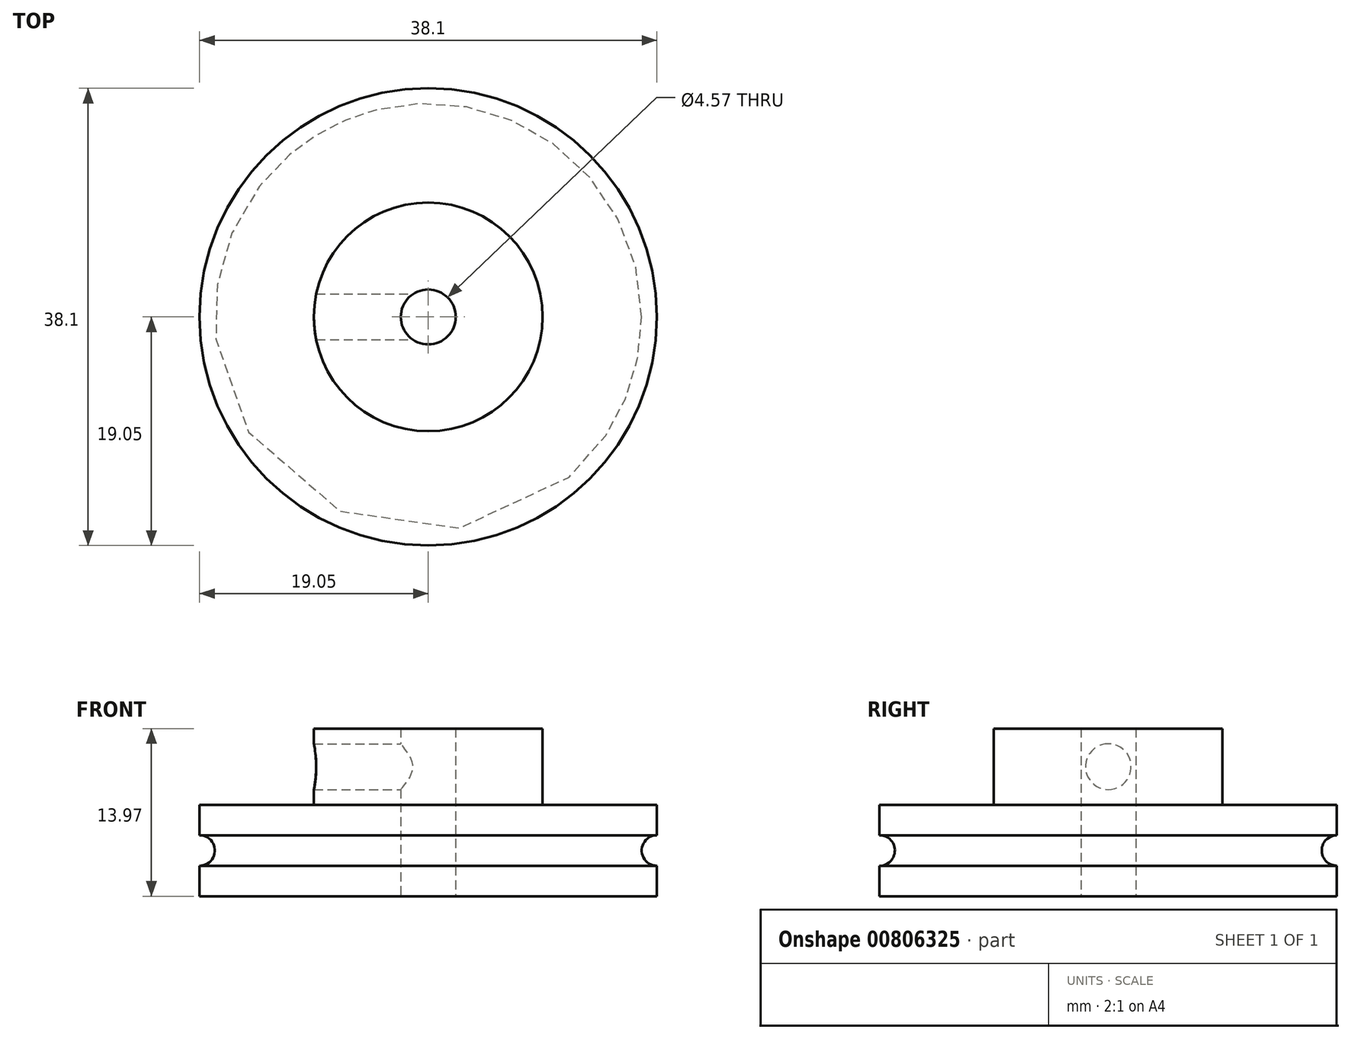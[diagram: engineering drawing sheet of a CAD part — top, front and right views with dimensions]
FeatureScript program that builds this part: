
annotation { "Feature Type Name" : "Feature", "Feature Type Description" : "" }
export const myFeature = defineFeature(function(context is Context, id is Id, definition is map)
    precondition{}
    {
        {
            var Q0;
            Q0=qCreatedBy(makeId("Top.planeOp"),FACE);
            var sketch = newSketch(context, id + "F0", { "sketchPlane" : qUnion([Q0])});
            skCircle(sketch, "E0", {"center": v(0, 0) * mm, "radius": 19.05 * mm});
            skSolve(sketch);
        }
        {
            var Q0;
            Q0=makeQuery(id+"F0.imprint","IMPRINT",FACE,{"disambiguationData":[TD([[makeQuery(id+"F0.imprint","IMPRINT",EDGE,{"derivedFrom":sQuery(id+"F0.wireOp",EDGE,"E0")}),1.0]])]});
            extrude(context, id + "F1", {"entities" : qUnion([Q0]), "depth" : 7.62 * mm, "offsetDistance" : 25.4 * mm});
        }
        {
            var Q0;
            Q0=makeQuery(id+"F1.opExtrude","CAP_FACE",FACE,{"disambiguationData":[OSD([sQuery(id+"F0.wireOp",EDGE,"E0")])],"isStart":false});
            var sketch = newSketch(context, id + "F2", { "sketchPlane" : qUnion([Q0])});
            skCircle(sketch, "E1", {"center": v(0, 0) * mm, "radius": 9.53 * mm});
            skSolve(sketch);
        }
        {
            var Q0;
            Q0=makeQuery(id+"F2.imprint","IMPRINT",FACE,{"disambiguationData":[TD([[makeQuery(id+"F2.imprint","IMPRINT",EDGE,{"derivedFrom":sQuery(id+"F2.wireOp",EDGE,"E1")}),1.0]])]});
            extrude(context, id + "F3", {"entities" : qUnion([Q0]), "operationType" : NewBodyOperationType.ADD, "depth" : 6.35 * mm, "offsetDistance" : 25.4 * mm});
        }
        {
            var Q0;
            Q0=qCreatedBy(makeId("Right.planeOp"),FACE);
            var sketch = newSketch(context, id + "F4", { "sketchPlane" : qUnion([Q0])});
            skCircle(sketch, "E2", {"center": v(0, 10.8) * mm, "radius": 1.9 * mm});
            skSolve(sketch);
        }
        {
            var Q0;
            Q0 = qSketchRegion(id + "F4", true);
            extrude(context, id + "F5", {"entities" : qUnion([Q0]), "operationType" : NewBodyOperationType.REMOVE, "oppositeDirection" : true, "depth" : 25.4 * mm, "offsetDistance" : 25.4 * mm});
        }
        {
            var Q0;
            Q0=makeQuery(id+"F1.opExtrude","CAP_FACE",FACE,{"disambiguationData":[OSD([sQuery(id+"F0.wireOp",EDGE,"E0")])],"isStart":true});
            var sketch = newSketch(context, id + "F6", { "sketchPlane" : qUnion([Q0])});
            skCircle(sketch, "E3", {"center": v(0, 0) * mm, "radius": 2.29 * mm});
            skSolve(sketch);
        }
        {
            var Q0;
            Q0=makeQuery(id+"F6.imprint","IMPRINT",FACE,{"disambiguationData":[TD([[makeQuery(id+"F6.imprint","IMPRINT",EDGE,{"derivedFrom":sQuery(id+"F6.wireOp",EDGE,"E3")}),1.0]])]});
            extrude(context, id + "F7", {"entities" : qUnion([Q0]), "operationType" : NewBodyOperationType.REMOVE, "oppositeDirection" : true, "depth" : 101.6 * mm, "offsetDistance" : 25.4 * mm});
        }
        {
            var Q0;
            Q0=qCreatedBy(makeId("Right.planeOp"),FACE);
            var sketch = newSketch(context, id + "F8", { "sketchPlane" : qUnion([Q0])});
            skCircle(sketch, "E4", {"center": v(-19.05, 3.81) * mm, "radius": 1.27 * mm});
            skSolve(sketch);
        }
        {
            var Q0;
            Q0=makeQuery(id+"F8.imprint","IMPRINT",FACE,{"disambiguationData":[TD([[makeQuery(id+"F8.imprint","IMPRINT",EDGE,{"derivedFrom":sQuery(id+"F8.wireOp",EDGE,"E4")}),1.0]])]});
            var Q1;
            Q1=makeQuery(id+"F3.opExtrude","CAP_EDGE",EDGE,{"disambiguationData":[OSD([sQuery(id+"F2.wireOp",EDGE,"E1")])],"isStart":false});
            revolve(context, id + "F9", {"operationType" : NewBodyOperationType.REMOVE, "surfaceOperationType" : NewSurfaceOperationType.NEW, "entities" : qUnion([Q0]), "axis" : qUnion([Q1]), "revolveType" : RevolveType.FULL, "oppositeDirection" : true});
        }
    });
